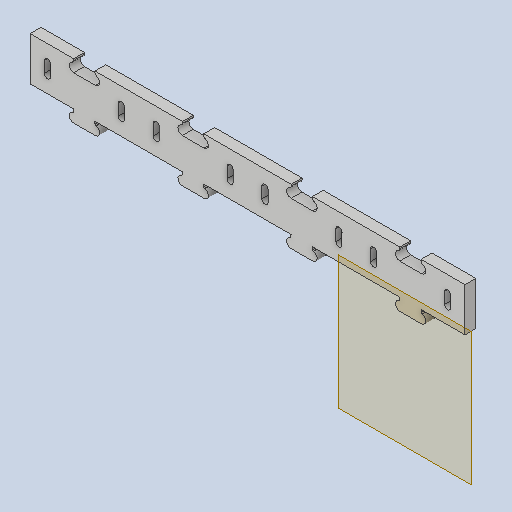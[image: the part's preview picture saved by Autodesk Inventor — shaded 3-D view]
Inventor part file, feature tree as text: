
AUTODESK INVENTOR PART (.ipt)
format: ipt  version: 2022 (Build 260153000, 153)  size: 329,216 bytes
history: native  units: mm
features: reference x5, other x5, extrude x3, sketch x3, projected_geometry x2, plane x1, fillet x1, pattern_linear x1
ambient origin geometry x8: Origin, YZ Plane, XZ Plane, XY Plane, X Axis, Y Axis, Z Axis, Center Point
bodies: Solid1 (feature_tree)
feature tree (21):
  plane  "Work Plane1"
  extrude  "Extrusion1"  Depth=25.0mm
  extrude  "Extrusion2"  Depth=5.0mm TaperAngle=0.0deg
  fillet  "Fillet1"  Radius=2.023mm
  extrude  "Extrusion3"  TaperAngle=0.0deg  [1 undecoded]
  pattern_linear  "Rectangular Pattern1"  Spacing1=3.6mm  [1 undecoded]
  sketch  "Sketch1"  dims[d0=25.0mm d1=25.0mm]
  reference  "Reference1"
  reference  "Reference5"
  sketch  "Sketch2"  dims[d2=0.05mm d3=5.0mm d4=0.0mm d5=2.023mm]
  reference  "Reference6"
  projected_geometry  "Projected Loop1"
  projected_geometry  "Projected Loop2"
  reference  "Reference7"
  sketch  "Sketch3"  dims[d6=0.0mm d7=0.0mm d8=3.6mm d9=0.0mm d10=0.1mm d11=0.0mm d12=5.0mm d13=0.0mm d14=1.0mm d15=2.9mm d16=2.8mm d17=8.0mm d18=8.0mm d19=5.0mm d20=0.0mm d21=0.0mm d22=40.0mm d24=50.0mm d25=2.3mm d26=2.9mm]
  reference  "Reference8"
  other  "Assembly_Hi2_Uppsala_v3.iam"
  other  "Application_Fluorescence_Microscope_Infinity_v3:1"
  other  "10_Base_puzzle_v3:13"
  other  "Assembly_neje_slide_y_wellplateholder_20mmrod:1"
  other  "Neje_Base_Rod_20mm:2"
note: 2 required parameter values undecoded (feature->parameter linkage not recoverable at this tier; creation-order binding heuristic only, values carry confidence <= 0.55)
